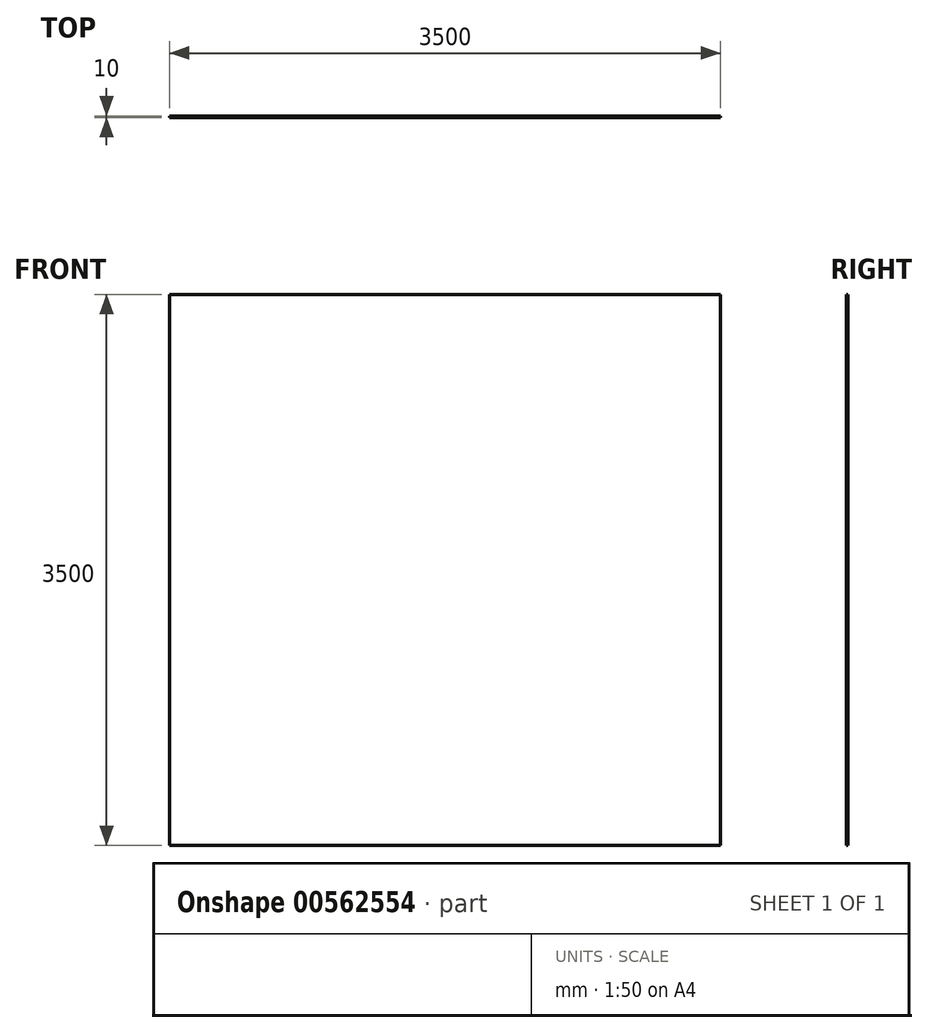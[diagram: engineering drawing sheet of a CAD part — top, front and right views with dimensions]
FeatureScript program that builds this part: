
annotation { "Feature Type Name" : "Feature", "Feature Type Description" : "" }
export const myFeature = defineFeature(function(context is Context, id is Id, definition is map)
    precondition{}
    {
        {
            var Q0;
            Q0=qCreatedBy(makeId("Front.planeOp"),FACE);
            var sketch = newSketch(context, id + "F0", { "sketchPlane" : qUnion([Q0])});
            skLineSegment(sketch, "E0.bottom", {"start": v(0, 0) * mm, "end": v(3500, 0) * mm});
            skLineSegment(sketch, "E0.top", {"start": v(0, 3500) * mm, "end": v(3500, 3500) * mm});
            skLineSegment(sketch, "E0.left", {"start": v(0, 0) * mm, "end": v(0, 3500) * mm});
            skLineSegment(sketch, "E0.right", {"start": v(3500, 0) * mm, "end": v(3500, 3500) * mm});
            skSolve(sketch);
        }
        {
            var Q0;
            Q0=makeQuery(id+"F0.imprint","IMPRINT",FACE,{"disambiguationData":[TD([[makeQuery(id+"F0.imprint","IMPRINT",EDGE,{"derivedFrom":sQuery(id+"F0.wireOp",EDGE,"E0.bottom")}),1.0]])]});
            extrude(context, id + "F1", {"entities" : qUnion([Q0]), "depth" : 10 * mm, "offsetDistance" : 25 * mm});
        }
    });
